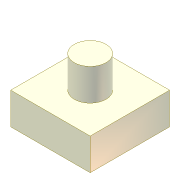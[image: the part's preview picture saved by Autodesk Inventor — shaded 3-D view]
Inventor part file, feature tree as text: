
AUTODESK INVENTOR PART (.ipt)
format: ipt  version: unknown  size: 162,816 bytes
history: native  units: mm
features: extrude x2, sketch x2
ambient origin geometry x8: Origin, YZ Plane, XZ Plane, XY Plane, X Axis, Y Axis, Z Axis, Center Point
feature tree (4):
  extrude  "Extrusion1"  Depth=10.0mm
  extrude  "Extrusion2"  Depth=8.0mm TaperAngle=0.0deg
  sketch  "Sketch1"  dims[d0=4.0mm d1=10.0mm]
  sketch  "Sketch2"  dims[d2=4.0mm d3=0.0mm d4=8.0mm d5=0.0mm]
